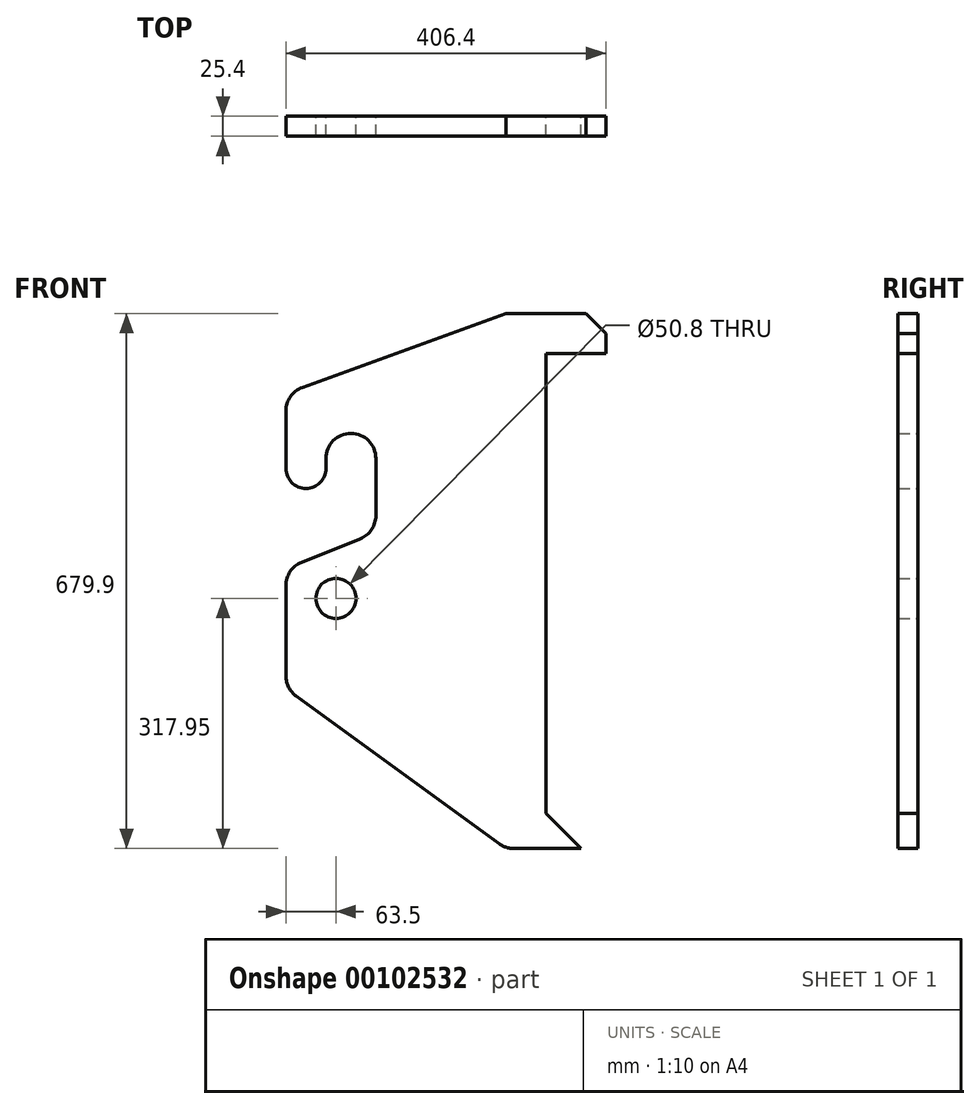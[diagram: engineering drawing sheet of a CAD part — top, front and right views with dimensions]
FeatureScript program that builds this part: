
annotation { "Feature Type Name" : "Feature", "Feature Type Description" : "" }
export const myFeature = defineFeature(function(context is Context, id is Id, definition is map)
    precondition{}
    {
        {
            var Q0;
            Q0=qCreatedBy(makeId("Front.planeOp"),FACE);
            var sketch = newSketch(context, id + "F0", { "sketchPlane" : qUnion([Q0])});
            skArc(sketch, "E0", {"start": v(-215.9, -184.15) * mm, "mid": v(-247.65, -152.4) * mm, "end": v(-279.4, -184.15) * mm});
            skLineSegment(sketch, "E1", {"start": v(0, 0) * mm, "end": v(50.8, 0) * mm});
            skLineSegment(sketch, "E2", {"start": v(76.2, -25.4) * mm, "end": v(76.2, -50.8) * mm});
            skLineSegment(sketch, "E3", {"start": v(76.2, -50.8) * mm, "end": v(0, -50.8) * mm});
            skLineSegment(sketch, "E4", {"start": v(0, -50.8) * mm, "end": v(0, -635) * mm});
            skLineSegment(sketch, "E5", {"start": v(0, -635) * mm, "end": v(44.9, -679.9) * mm});
            skLineSegment(sketch, "E6", {"start": v(50.8, 0) * mm, "end": v(76.2, -25.4) * mm});
            skPoint(sketch, "E7.orphan", {"position": v(76.2, 0) * mm});
            skCircle(sketch, "E8", {"center": v(-266.7, -361.95) * mm, "radius": 25.4 * mm});
            skArc(sketch, "E9", {"start": v(-330.2, -196.85) * mm, "mid": v(-304.8, -222.25) * mm, "end": v(-279.4, -196.85) * mm});
            skLineSegment(sketch, "E10", {"start": v(0, 0) * mm, "end": v(-50.8, 0) * mm});
            skLineSegment(sketch, "E11", {"start": v(-50.8, 0) * mm, "end": v(-309.3, -94) * mm});
            skLineSegment(sketch, "E12", {"start": v(-330.2, -123.84) * mm, "end": v(-330.2, -196.85) * mm});
            skLineSegment(sketch, "E13", {"start": v(-279.4, -184.15) * mm, "end": v(-279.4, -196.85) * mm});
            skLineSegment(sketch, "E14", {"start": v(44.9, -679.9) * mm, "end": v(-40.48, -679.9) * mm});
            skLineSegment(sketch, "E15", {"start": v(-59.15, -673.83) * mm, "end": v(-317.12, -486.21) * mm});
            skLineSegment(sketch, "E16", {"start": v(-330.2, -460.53) * mm, "end": v(-330.2, -345.75) * mm});
            skLineSegment(sketch, "E17", {"start": v(-215.9, -184.15) * mm, "end": v(-215.9, -256.86) * mm});
            skLineSegment(sketch, "E18", {"start": v(-310.3, -316.3) * mm, "end": v(-235.8, -286.32) * mm});
            skPoint(sketch, "E19.visualSharp", {"position": v(-330.2, -324.3) * mm});
            skArc(sketch, "E19.filletArc", {"start": v(-310.3, -316.3) * mm, "mid": v(-324.76, -327.98) * mm, "end": v(-330.2, -345.75) * mm});
            skPoint(sketch, "E20.visualSharp", {"position": v(-330.2, -101.6) * mm});
            skArc(sketch, "E20.filletArc", {"start": v(-309.3, -94) * mm, "mid": v(-324.46, -105.62) * mm, "end": v(-330.2, -123.84) * mm});
            skPoint(sketch, "E21.visualSharp", {"position": v(-215.9, -278.3) * mm});
            skArc(sketch, "E21.filletArc", {"start": v(-235.8, -286.32) * mm, "mid": v(-221.34, -274.63) * mm, "end": v(-215.9, -256.86) * mm});
            skPoint(sketch, "E22.visualSharp", {"position": v(-330.2, -476.7) * mm});
            skArc(sketch, "E22.filletArc", {"start": v(-330.2, -460.53) * mm, "mid": v(-326.74, -474.94) * mm, "end": v(-317.12, -486.21) * mm});
            skPoint(sketch, "E23.visualSharp", {"position": v(-50.8, -679.9) * mm});
            skArc(sketch, "E23.filletArc", {"start": v(-59.15, -673.83) * mm, "mid": v(-50.3, -678.34) * mm, "end": v(-40.48, -679.9) * mm});
            skSolve(sketch);
        }
        {
            var Q0;
            Q0=makeQuery(id+"F0.imprint","IMPRINT",FACE,{"disambiguationData":[TD([[makeQuery(id+"F0.imprint","IMPRINT",EDGE,{"derivedFrom":sQuery(id+"F0.wireOp",EDGE,"E0")}),-1.0]])]});
            extrude(context, id + "F1", {"entities" : qUnion([Q0]), "depth" : 25.4 * mm});
        }
    });
